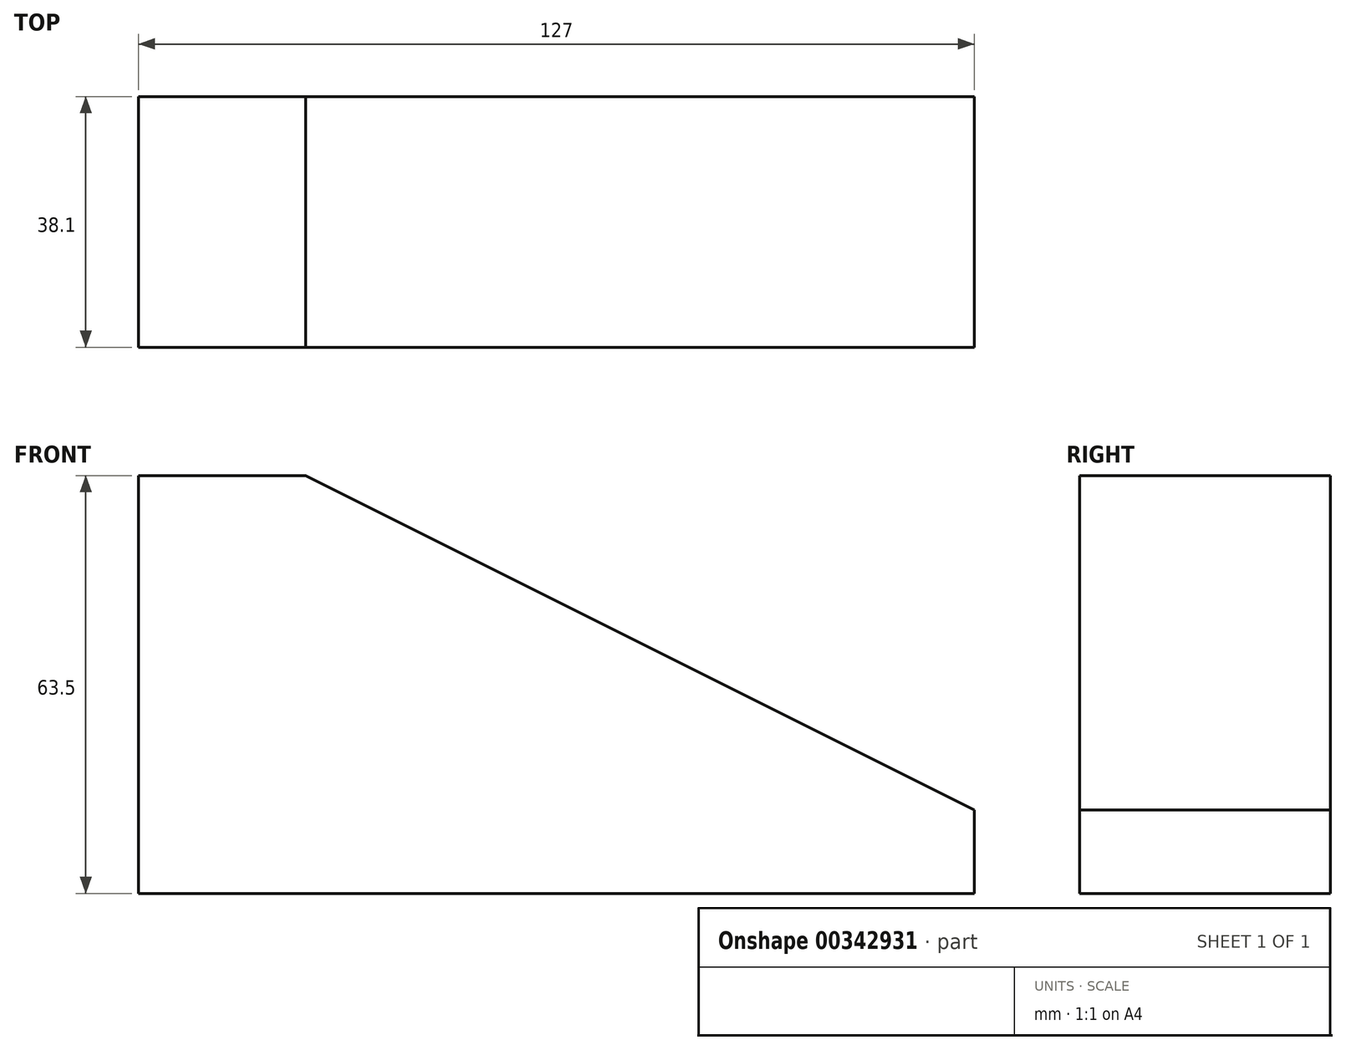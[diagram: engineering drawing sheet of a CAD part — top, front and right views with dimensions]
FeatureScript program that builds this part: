
annotation { "Feature Type Name" : "Feature", "Feature Type Description" : "" }
export const myFeature = defineFeature(function(context is Context, id is Id, definition is map)
    precondition{}
    {
        {
            var Q0;
            Q0=qCreatedBy(makeId("Front.planeOp"),FACE);
            var sketch = newSketch(context, id + "F0", { "sketchPlane" : qUnion([Q0])});
            skLineSegment(sketch, "E0", {"start": v(-53.94, 50.8) * mm, "end": v(-28.54, 50.8) * mm});
            skLineSegment(sketch, "E1", {"start": v(-53.94, 50.8) * mm, "end": v(-53.94, -12.7) * mm});
            skLineSegment(sketch, "E2", {"start": v(-53.94, -12.7) * mm, "end": v(73.06, -12.7) * mm});
            skLineSegment(sketch, "E3", {"start": v(73.06, -12.7) * mm, "end": v(73.06, 0) * mm});
            skLineSegment(sketch, "E4", {"start": v(-28.54, 50.8) * mm, "end": v(73.06, 0) * mm});
            skSolve(sketch);
        }
        {
            var Q0;
            Q0 = qSketchRegion(id + "F0", true);
            extrude(context, id + "F1", {"entities" : qUnion([Q0]), "depth" : 38.1 * mm});
        }
    });
